# Revit family: merry_christmas_tree
name_source: partatom
category: Generic Models
units: mm (PartAtom-declared; Revit-internal decimal feet)

## family parameters
Always vertical = No
Can host rebar = No
Cut with Voids When Loaded = No
Part Type = Normal
Room Calculation Point = No
Round Connector Dimension = Use Diameter
Shared = No
Work Plane-Based = No

## types (1)
- Default
    BIMobject category = Other
    BOSUseNativeGeometries = 1
    Date of publishing = 12/25/2015
    Default Elevation = 0' - 0"
    Design country = Sweden
    Edition number = 1
    IFC Classification = Furnishing Element
    Manufacturer country = Sweden
    Manufacturer name = BIMobject (Demo)
    Material main = Wood
    Material secondary = Acrylic
    Nominal height = 3500
    Nominal width = 1000
    Product Guid = 545aa80a-897b-42e6-8cdb-9b55cc002c21
    Product SKU = xmastree
    Product data url = https://bimobject.com
    Product family = Charity
    Product group = Children of the World
    Product name = Merry Christmas Tree
    QR code = http://bimobject.com
    UNSPSC Code = 391016
    Weight Net (Kg) = 17

## geometry (parser evidence)
native form markers: Sweep x3
no freeform markers — native parametric forms only
